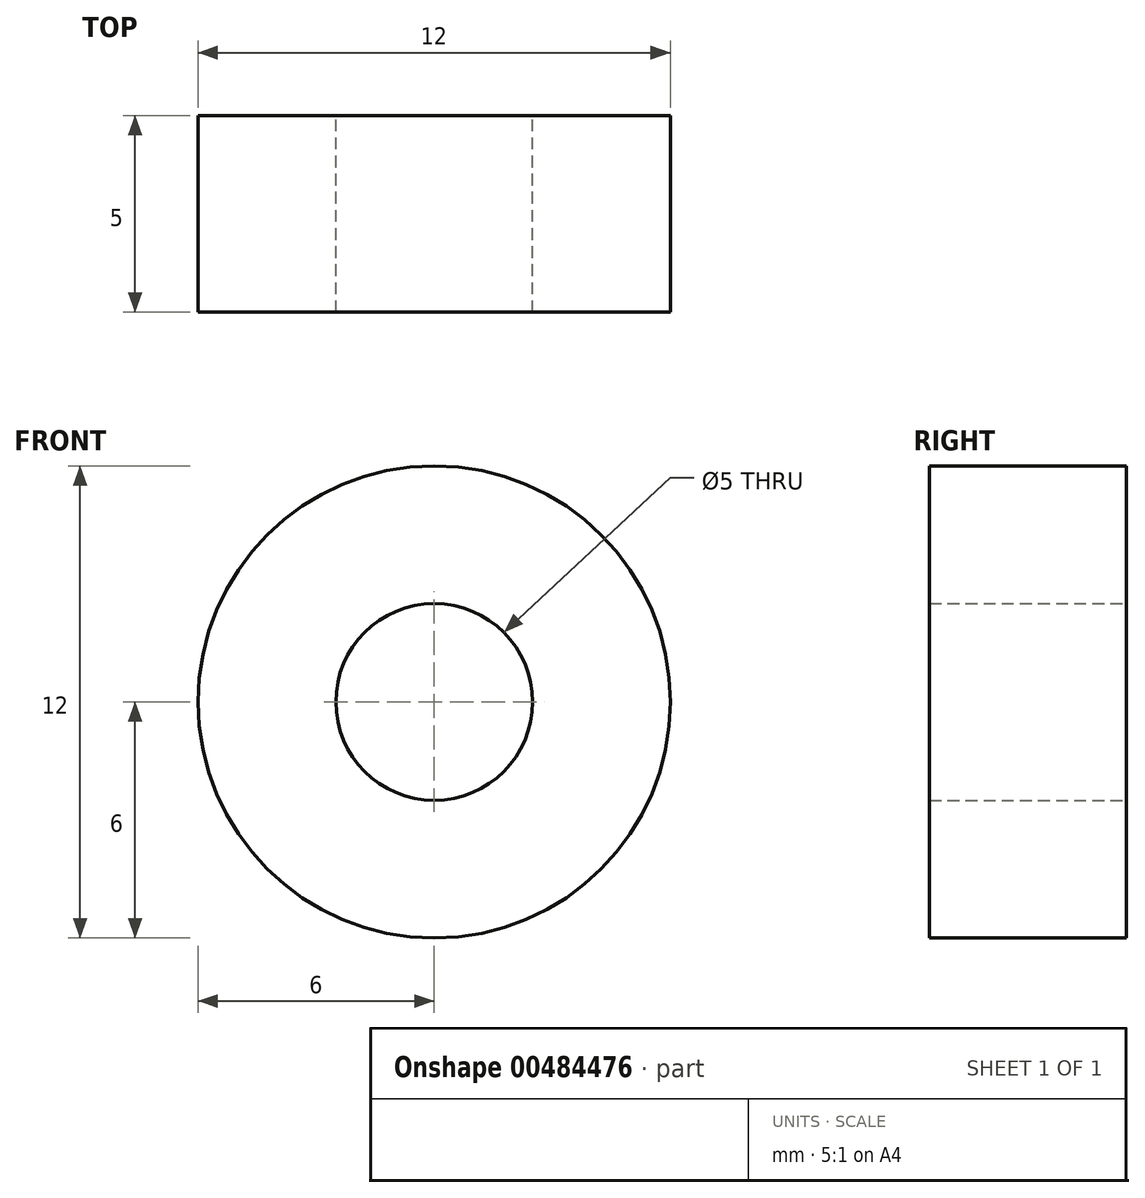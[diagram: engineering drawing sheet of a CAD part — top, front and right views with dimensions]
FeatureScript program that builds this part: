
annotation { "Feature Type Name" : "Feature", "Feature Type Description" : "" }
export const myFeature = defineFeature(function(context is Context, id is Id, definition is map)
    precondition{}
    {
        {
            var Q0;
            Q0=qCreatedBy(makeId("Front.planeOp"),FACE);
            var sketch = newSketch(context, id + "F0", { "sketchPlane" : qUnion([Q0])});
            skCircle(sketch, "E0", {"center": v(0, 0) * mm, "radius": 6 * mm});
            skCircle(sketch, "E1", {"center": v(0, 0) * mm, "radius": 2.5 * mm});
            skSolve(sketch);
        }
        {
            var Q0;
            Q0=makeQuery(id+"F0.imprint","IMPRINT",FACE,{"disambiguationData":[TD([[makeQuery(id+"F0.imprint","IMPRINT",EDGE,{"derivedFrom":sQuery(id+"F0.wireOp",EDGE,"E0")}),1.0]])]});
            var Q1;
            Q1=sQuery(id+"F0.wireOp",EDGE,"E0");
            extrude(context, id + "F1", {"entities" : qUnion([Q0]), "surfaceEntities" : qUnion([Q1]), "depth" : 5 * mm});
        }
        {
            var Q0;
            Q0=makeQuery(id+"F1.opExtrude","SWEPT_BODY",BODY,{"disambiguationData":[OSD([sQuery(id+"F0.wireOp",EDGE,"E0")])]});
            transform(context, id + "F2", {"entities" : qUnion([Q0]), "transformType" : TransformType.TRANSLATION_3D, "dx" : 0 * mm, "dy" : 0 * mm, "dz" : 0 * mm, "makeCopy" : true});
        }
        {
            var Q0;
            Q0=makeQuery(id+"F2.opPattern","COPY",BODY,{"derivedFrom":makeQuery(id+"F1.opExtrude","SWEPT_BODY",BODY,{"disambiguationData":[OSD([sQuery(id+"F0.wireOp",EDGE,"E0")])]}),"instanceName":"1"});
            deleteBodies(context, id + "F3", {"entities" : qUnion([Q0])});
        }
    });
